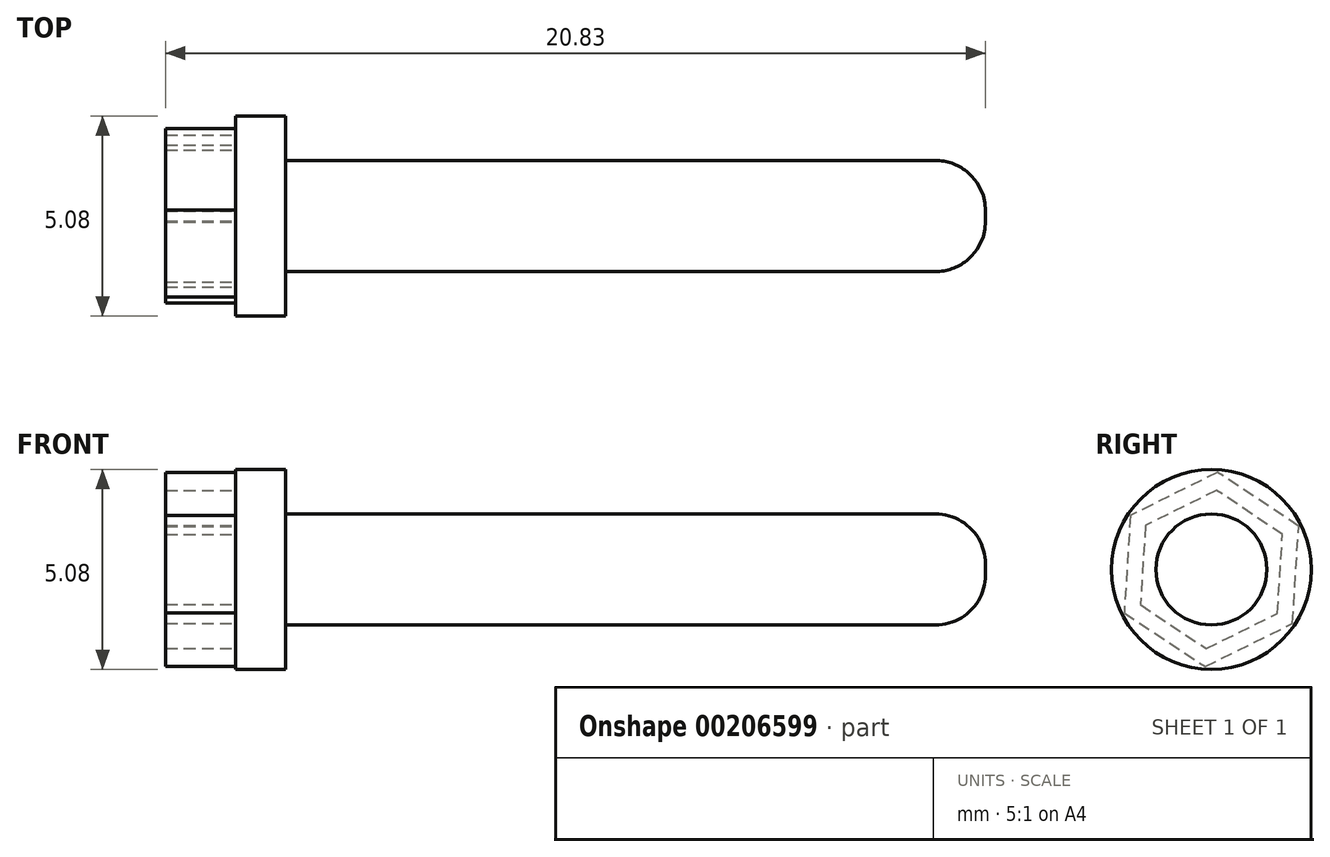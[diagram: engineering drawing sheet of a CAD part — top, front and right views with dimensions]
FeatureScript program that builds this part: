
annotation { "Feature Type Name" : "Feature", "Feature Type Description" : "" }
export const myFeature = defineFeature(function(context is Context, id is Id, definition is map)
    precondition{}
    {
        {
            var Q0;
            Q0=qCreatedBy(makeId("Right.planeOp"),FACE);
            var sketch = newSketch(context, id + "F0", { "sketchPlane" : qUnion([Q0])});
            skCircle(sketch, "E0", {"center": v(0, 0) * mm, "radius": 2.54 * mm});
            skSolve(sketch);
        }
        {
            var Q0;
            Q0=makeQuery(id+"F0.imprint","IMPRINT",FACE,{"disambiguationData":[TD([[makeQuery(id+"F0.imprint","IMPRINT",EDGE,{"derivedFrom":sQuery(id+"F0.wireOp",EDGE,"E0")}),1.0]])]});
            extrude(context, id + "F1", {"entities" : qUnion([Q0]), "depth" : 1.27 * mm});
        }
        {
            var Q0;
            Q0=makeQuery(id+"F1.opExtrude","CAP_FACE",FACE,{"disambiguationData":[OSD([sQuery(id+"F0.wireOp",EDGE,"E0")])],"isStart":true});
            var sketch = newSketch(context, id + "F2", { "sketchPlane" : qUnion([Q0])});
            skCircle(sketch, "E1.cCircle", {"center": v(0, 0) * mm, "radius": 2.14 * mm, "construction": true});
            skLineSegment(sketch, "E1.0", {"start": v(0.16, -2.47) * mm, "end": v(-2.06, -1.37) * mm});
            skLineSegment(sketch, "E1.1", {"start": v(-2.06, -1.37) * mm, "end": v(-2.22, 1.1) * mm});
            skLineSegment(sketch, "E1.2", {"start": v(-2.22, 1.1) * mm, "end": v(-0.16, 2.47) * mm});
            skLineSegment(sketch, "E1.3", {"start": v(-0.16, 2.47) * mm, "end": v(2.06, 1.37) * mm});
            skLineSegment(sketch, "E1.4", {"start": v(2.06, 1.37) * mm, "end": v(2.22, -1.1) * mm});
            skLineSegment(sketch, "E1.5", {"start": v(2.22, -1.1) * mm, "end": v(0.16, -2.47) * mm});
            skPoint(sketch, "E1.0.midPoint", {"position": v(-0.95, -1.92) * mm});
            skCircle(sketch, "E2.cCircle", {"center": v(0, 0) * mm, "radius": 1.74 * mm, "construction": true});
            skLineSegment(sketch, "E2.0", {"start": v(0.13, -2.01) * mm, "end": v(-1.68, -1.12) * mm});
            skLineSegment(sketch, "E2.1", {"start": v(-1.68, -1.12) * mm, "end": v(-1.8, 0.9) * mm});
            skLineSegment(sketch, "E2.2", {"start": v(-1.8, 0.9) * mm, "end": v(-0.13, 2.01) * mm});
            skLineSegment(sketch, "E2.3", {"start": v(-0.13, 2.01) * mm, "end": v(1.68, 1.12) * mm});
            skLineSegment(sketch, "E2.4", {"start": v(1.68, 1.12) * mm, "end": v(1.8, -0.9) * mm});
            skLineSegment(sketch, "E2.5", {"start": v(1.8, -0.9) * mm, "end": v(0.13, -2.01) * mm});
            skPoint(sketch, "E2.0.midPoint", {"position": v(-0.77, -1.56) * mm});
            skSolve(sketch);
        }
        {
            var Q0;
            Q0=makeQuery(id+"F2.imprint","IMPRINT",FACE,{"disambiguationData":[TD([[makeQuery(id+"F2.imprint","IMPRINT",EDGE,{"derivedFrom":sQuery(id+"F2.wireOp",EDGE,"E1.0")}),-1.0]])]});
            extrude(context, id + "F3", {"entities" : qUnion([Q0]), "operationType" : NewBodyOperationType.ADD, "depth" : 1.78 * mm});
        }
        {
            var Q0;
            Q0=makeQuery(id+"F1.opExtrude","CAP_FACE",FACE,{"disambiguationData":[OSD([sQuery(id+"F0.wireOp",EDGE,"E0")])],"isStart":false});
            var sketch = newSketch(context, id + "F4", { "sketchPlane" : qUnion([Q0])});
            skCircle(sketch, "E3", {"center": v(0, 0) * mm, "radius": 1.4 * mm});
            skSolve(sketch);
        }
        {
            var Q0;
            Q0=makeQuery(id+"F4.imprint","IMPRINT",FACE,{"disambiguationData":[TD([[makeQuery(id+"F4.imprint","IMPRINT",EDGE,{"derivedFrom":sQuery(id+"F4.wireOp",EDGE,"E3")}),1.0]])]});
            extrude(context, id + "F5", {"entities" : qUnion([Q0]), "operationType" : NewBodyOperationType.ADD, "depth" : 17.78 * mm});
        }
        {
            var Q0;
            Q0=makeQuery(id+"F5.opExtrude","CAP_FACE",FACE,{"disambiguationData":[OSD([sQuery(id+"F4.wireOp",EDGE,"E3")])],"isStart":false});
            fillet(context, id + "F6", {"entities" : qUnion([Q0]), "radius" : 1.27 * mm, "tangentPropagation" : true, "allowEdgeOverflow" : false});
        }
    });
